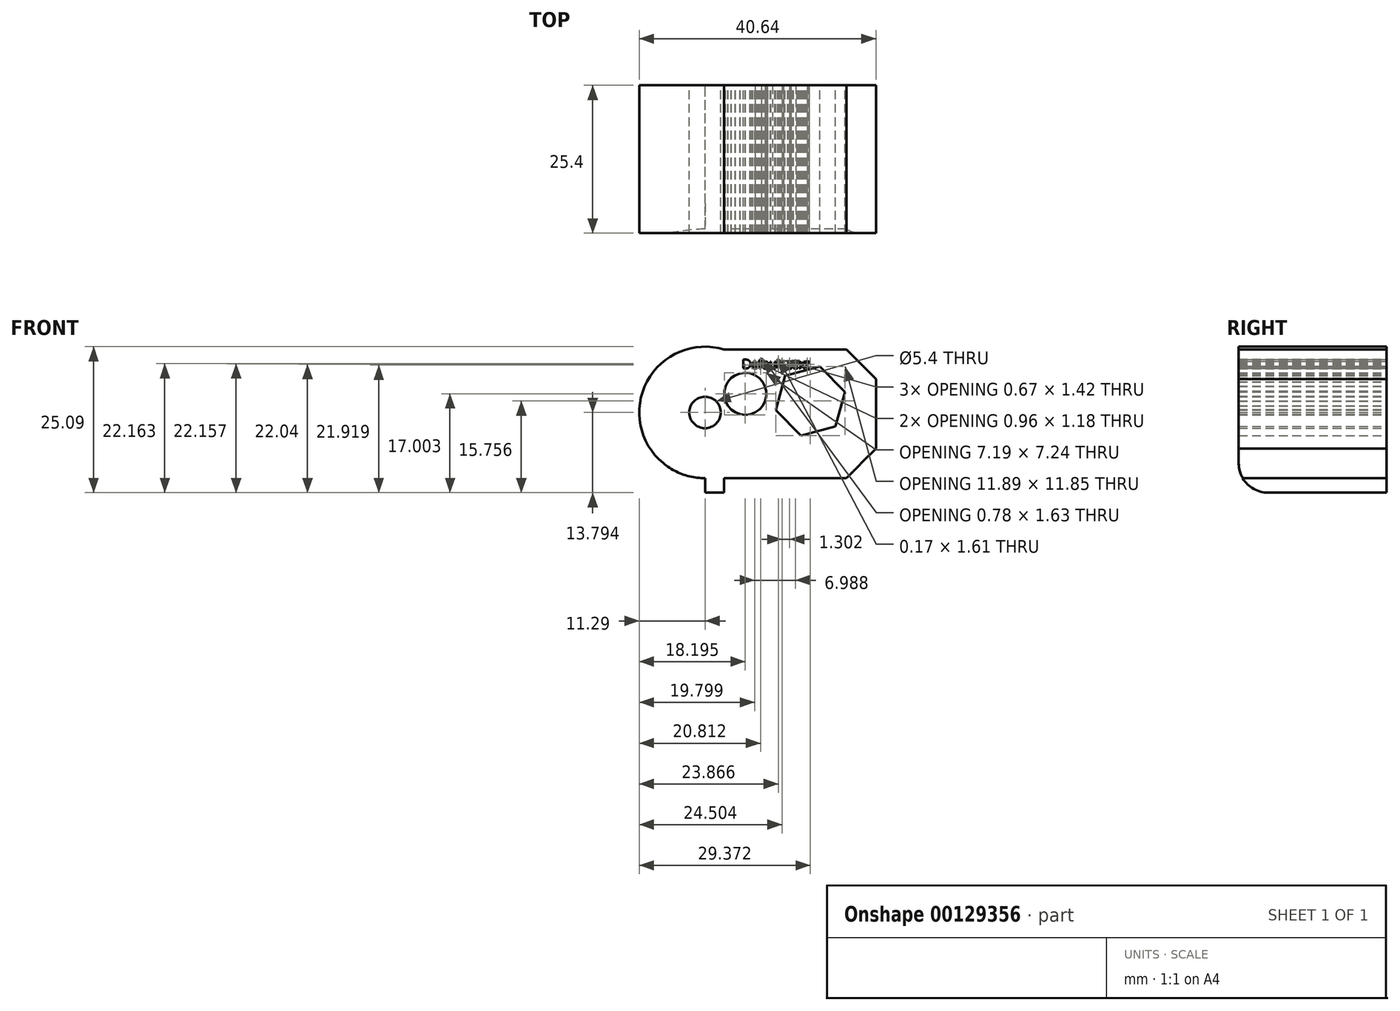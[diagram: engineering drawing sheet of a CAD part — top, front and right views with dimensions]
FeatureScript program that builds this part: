
annotation { "Feature Type Name" : "Feature", "Feature Type Description" : "" }
export const myFeature = defineFeature(function(context is Context, id is Id, definition is map)
    precondition{}
    {
        {
            var Q0;
            Q0=qCreatedBy(makeId("Front.planeOp"),FACE);
            var sketch = newSketch(context, id + "F0", { "sketchPlane" : qUnion([Q0])});
            skLineSegment(sketch, "E0.bottom", {"start": v(0, 0) * mm, "end": v(3.28, 0) * mm});
            skLineSegment(sketch, "E0.left", {"start": v(0, 0) * mm, "end": v(0, 2.5) * mm});
            skLineSegment(sketch, "E0.right", {"start": v(3.28, 0) * mm, "end": v(3.28, 2.5) * mm});
            skLineSegment(sketch, "E1.bottom", {"start": v(3.28, 2.5) * mm, "end": v(29.35, 2.5) * mm});
            skLineSegment(sketch, "E1.top", {"start": v(3.28, 24.6) * mm, "end": v(29.35, 24.6) * mm});
            skLineSegment(sketch, "E1.right", {"start": v(29.35, 2.5) * mm, "end": v(29.35, 24.6) * mm});
            skArc(sketch, "E2", {"start": v(3.28, 24.6) * mm, "mid": v(-11.17, 15.45) * mm, "end": v(0, 2.5) * mm});
            skCircle(sketch, "E3.cCircle", {"center": v(6.9, 17) * mm, "radius": 3.6 * mm, "construction": true});
            skLineSegment(sketch, "E3.0", {"start": v(9.33, 14.32) * mm, "end": v(8.62, 13.82) * mm});
            skLineSegment(sketch, "E3.1", {"start": v(8.62, 13.82) * mm, "end": v(7.8, 13.5) * mm});
            skLineSegment(sketch, "E3.2", {"start": v(7.8, 13.5) * mm, "end": v(6.94, 13.39) * mm});
            skLineSegment(sketch, "E3.3", {"start": v(6.94, 13.39) * mm, "end": v(6.08, 13.48) * mm});
            skLineSegment(sketch, "E3.4", {"start": v(6.08, 13.48) * mm, "end": v(5.26, 13.78) * mm});
            skLineSegment(sketch, "E3.5", {"start": v(5.26, 13.78) * mm, "end": v(4.53, 14.27) * mm});
            skLineSegment(sketch, "E3.6", {"start": v(4.53, 14.27) * mm, "end": v(3.95, 14.92) * mm});
            skLineSegment(sketch, "E3.7", {"start": v(3.95, 14.92) * mm, "end": v(3.54, 15.68) * mm});
            skLineSegment(sketch, "E3.8", {"start": v(3.54, 15.68) * mm, "end": v(3.32, 16.53) * mm});
            skLineSegment(sketch, "E3.9", {"start": v(3.32, 16.53) * mm, "end": v(3.3, 17.4) * mm});
            skLineSegment(sketch, "E3.10", {"start": v(3.3, 17.4) * mm, "end": v(3.5, 18.25) * mm});
            skLineSegment(sketch, "E3.11", {"start": v(3.5, 18.25) * mm, "end": v(3.9, 19.03) * mm});
            skLineSegment(sketch, "E3.12", {"start": v(3.9, 19.03) * mm, "end": v(4.48, 19.69) * mm});
            skLineSegment(sketch, "E3.13", {"start": v(4.48, 19.69) * mm, "end": v(5.19, 20.19) * mm});
            skLineSegment(sketch, "E3.14", {"start": v(5.19, 20.19) * mm, "end": v(6, 20.5) * mm});
            skLineSegment(sketch, "E3.15", {"start": v(6, 20.5) * mm, "end": v(6.87, 20.62) * mm});
            skLineSegment(sketch, "E3.16", {"start": v(6.87, 20.62) * mm, "end": v(7.73, 20.53) * mm});
            skLineSegment(sketch, "E3.17", {"start": v(7.73, 20.53) * mm, "end": v(8.55, 20.22) * mm});
            skLineSegment(sketch, "E3.18", {"start": v(8.55, 20.22) * mm, "end": v(9.28, 19.74) * mm});
            skLineSegment(sketch, "E3.19", {"start": v(9.28, 19.74) * mm, "end": v(9.86, 19.09) * mm});
            skLineSegment(sketch, "E3.20", {"start": v(9.86, 19.09) * mm, "end": v(10.27, 18.32) * mm});
            skLineSegment(sketch, "E3.21", {"start": v(10.27, 18.32) * mm, "end": v(10.5, 17.48) * mm});
            skLineSegment(sketch, "E3.22", {"start": v(10.5, 17.48) * mm, "end": v(10.5, 16.6) * mm});
            skLineSegment(sketch, "E3.23", {"start": v(10.5, 16.6) * mm, "end": v(10.3, 15.76) * mm});
            skLineSegment(sketch, "E3.24", {"start": v(10.3, 15.76) * mm, "end": v(9.9, 14.98) * mm});
            skLineSegment(sketch, "E3.25", {"start": v(9.9, 14.98) * mm, "end": v(9.33, 14.32) * mm});
            skPoint(sketch, "E3.0.midPoint", {"position": v(8.98, 14.07) * mm});
            skCircle(sketch, "E4.cCircle", {"center": v(18.08, 15.76) * mm, "radius": 5.32 * mm, "construction": true});
            skLineSegment(sketch, "E4.0", {"start": v(22.4, 11.38) * mm, "end": v(16.45, 9.83) * mm});
            skLineSegment(sketch, "E4.1", {"start": v(16.45, 9.83) * mm, "end": v(12.14, 14.2) * mm});
            skLineSegment(sketch, "E4.2", {"start": v(12.14, 14.2) * mm, "end": v(13.77, 20.13) * mm});
            skLineSegment(sketch, "E4.3", {"start": v(13.77, 20.13) * mm, "end": v(19.71, 21.68) * mm});
            skLineSegment(sketch, "E4.4", {"start": v(19.71, 21.68) * mm, "end": v(24.03, 17.3) * mm});
            skLineSegment(sketch, "E4.5", {"start": v(24.03, 17.3) * mm, "end": v(22.4, 11.38) * mm});
            skPoint(sketch, "E4.0.midPoint", {"position": v(19.42, 10.6) * mm});
            skCircle(sketch, "E5", {"center": v(0, 13.8) * mm, "radius": 2.7 * mm});
            skText(sketch, "E6", { "text": "Default text", "fontName": "OpenSans-Regular.ttf"});
            const initialGuessF0  = {"E6": [0.00636, 0.02135, 1, 0, 0.00153]};
            skSetInitialGuess(sketch, initialGuessF0);
            skSolve(sketch);
        }
        {
            var Q0;
            Q0=makeQuery(id+"F0.imprint","IMPRINT",FACE,{"disambiguationData":[TD([[makeQuery(id+"F0.imprint","IMPRINT",EDGE,{"derivedFrom":sQuery(id+"F0.wireOp",EDGE,"E0.bottom")}),1.0]])]});
            extrude(context, id + "F1", {"entities" : qUnion([Q0]), "depth" : 25.4 * mm});
        }
        {
            var Q0;
            Q0=makeQuery(id+"F1.opExtrude","SWEPT_EDGE",EDGE,{"disambiguationData":[OSD([sQuery(id+"F0.wireOp",EDGE,"E1.top"),sQuery(id+"F0.wireOp",EDGE,"E1.right")])]});
            var Q1;
            Q1=makeQuery(id+"F1.opExtrude","SWEPT_EDGE",EDGE,{"disambiguationData":[OSD([sQuery(id+"F0.wireOp",EDGE,"E1.bottom"),sQuery(id+"F0.wireOp",EDGE,"E1.right")])]});
            chamfer(context, id + "F2", {"entities" : qUnion([Q0, Q1]), "width" : 5.08 * mm, "tangentPropagation" : true});
        }
        {
            var Q0;
            Q0=makeQuery(id+"F1.opExtrude","CAP_EDGE",EDGE,{"disambiguationData":[OSD([sQuery(id+"F0.wireOp",EDGE,"E0.bottom")])],"isStart":false});
            fillet(context, id + "F3", {"entities" : qUnion([Q0]), "radius" : 5.08 * mm, "tangentPropagation" : true, "allowEdgeOverflow" : false});
        }
    });
